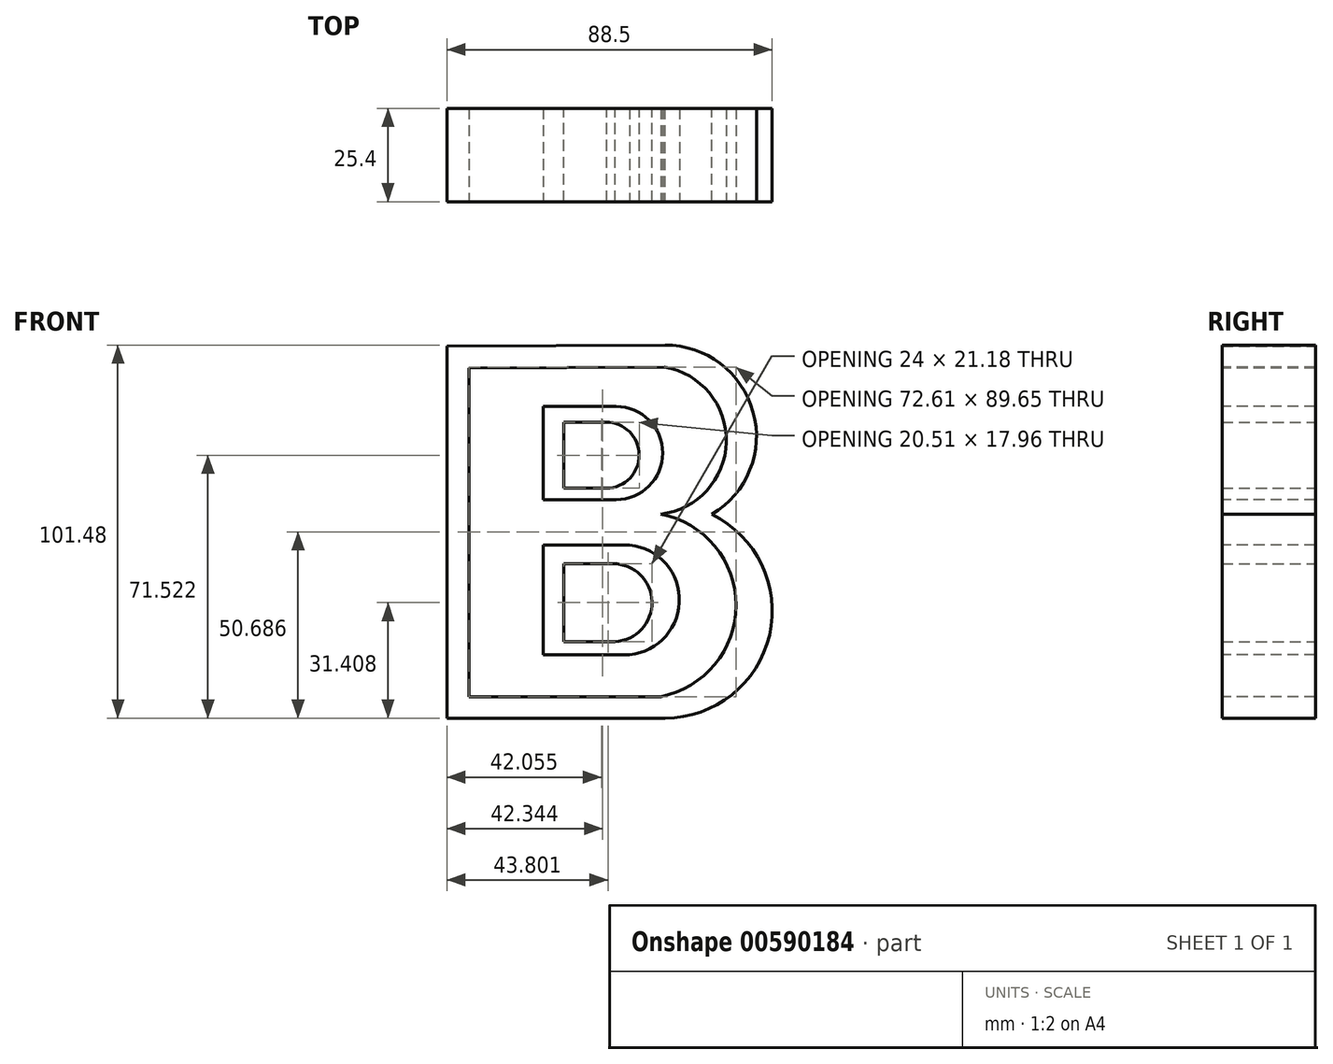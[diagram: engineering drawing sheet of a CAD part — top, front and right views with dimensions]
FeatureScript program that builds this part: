
annotation { "Feature Type Name" : "Feature", "Feature Type Description" : "" }
export const myFeature = defineFeature(function(context is Context, id is Id, definition is map)
    precondition{}
    {
        {
            var Q0;
            Q0=qCreatedBy(makeId("Front.planeOp"),FACE);
            var sketch = newSketch(context, id + "F0", { "sketchPlane" : qUnion([Q0])});
            skLineSegment(sketch, "E0", {"start": v(-89.9, 48.4) * mm, "end": v(-89.9, -52.82) * mm});
            skLineSegment(sketch, "E1", {"start": v(-89.9, -52.82) * mm, "end": v(-30.57, -52.82) * mm});
            skLineSegment(sketch, "E2", {"start": v(-30.57, 48.66) * mm, "end": v(-89.9, 48.4) * mm});
            skArc(sketch, "E3", {"start": v(-17.82, 2.6) * mm, "mid": v(-6.6, 30.5) * mm, "end": v(-30.57, 48.66) * mm});
            skArc(sketch, "E4", {"start": v(-30.57, -52.82) * mm, "mid": v(-2.14, -30.18) * mm, "end": v(-17.82, 2.6) * mm});
            skSolve(sketch);
        }
        {
            var Q0;
            Q0 = qSketchRegion(id + "F0", true);
            extrude(context, id + "F1", {"entities" : qUnion([Q0]), "depth" : 25.4 * mm, "offsetDistance" : 25.4 * mm});
        }
        {
            var Q0;
            Q0=makeQuery(id+"F0.imprint","IMPRINT",FACE,{"disambiguationData":[TD([[makeQuery(id+"F0.imprint","IMPRINT",EDGE,{"derivedFrom":sQuery(id+"F0.wireOp",EDGE,"E0")}),1.0]])]});
            var sketch = newSketch(context, id + "F2", { "sketchPlane" : qUnion([Q0])});
            skLineSegment(sketch, "E5", {"start": v(-58.1, 27.68) * mm, "end": v(-58.1, 9.72) * mm});
            skLineSegment(sketch, "E6", {"start": v(-58.1, 27.68) * mm, "end": v(-46.57, 27.68) * mm});
            skLineSegment(sketch, "E7", {"start": v(-58.1, 9.72) * mm, "end": v(-46.38, 9.72) * mm});
            skLineSegment(sketch, "E8", {"start": v(-58.1, -10.82) * mm, "end": v(-58.1, -32) * mm});
            skLineSegment(sketch, "E9", {"start": v(-58.1, -32) * mm, "end": v(-44.13, -32) * mm});
            skLineSegment(sketch, "E10", {"start": v(-58.1, -10.82) * mm, "end": v(-44.7, -10.82) * mm});
            skArc(sketch, "E11", {"start": v(-46.38, 9.72) * mm, "mid": v(-37.6, 18.8) * mm, "end": v(-46.57, 27.68) * mm});
            skArc(sketch, "E12", {"start": v(-44.13, -32) * mm, "mid": v(-34.1, -21.14) * mm, "end": v(-44.7, -10.82) * mm});
            skSolve(sketch);
        }
        {
            var Q0;
            Q0 = qSketchRegion(id + "F2", true);
            extrude(context, id + "F3", {"entities" : qUnion([Q0]), "operationType" : NewBodyOperationType.REMOVE, "oppositeDirection" : true, "depth" : 25.4 * mm, "offsetDistance" : 25.4 * mm});
        }
        {
            var Q0;
            Q0 = qSketchRegion(id + "F2", true);
            extrude(context, id + "F4", {"entities" : qUnion([Q0]), "operationType" : NewBodyOperationType.REMOVE, "depth" : 53.85 * mm, "offsetDistance" : 25.4 * mm});
        }
        {
            var Q0;
            Q0=makeQuery(id+"F1.opExtrude","CAP_FACE",FACE,{"disambiguationData":[OSD([sQuery(id+"F0.wireOp",EDGE,"E0"),sQuery(id+"F0.wireOp",EDGE,"E1"),sQuery(id+"F0.wireOp",EDGE,"E2"),sQuery(id+"F0.wireOp",EDGE,"E3"),sQuery(id+"F0.wireOp",EDGE,"E4")])],"isStart":false});
            var sketch = newSketch(context, id + "F5", { "sketchPlane" : qUnion([Q0])});
            skLineSegment(sketch, "E13", {"start": v(-83.86, 42.46) * mm, "end": v(-83.86, -46.96) * mm});
            skLineSegment(sketch, "E14", {"start": v(-83.86, -46.96) * mm, "end": v(-31.74, -46.96) * mm});
            skLineSegment(sketch, "E15", {"start": v(-83.86, 42.46) * mm, "end": v(-30.7, 42.7) * mm});
            skLineSegment(sketch, "E16", {"start": v(-63.67, 31.95) * mm, "end": v(-63.67, 6.6) * mm});
            skLineSegment(sketch, "E17", {"start": v(-63.67, 6.6) * mm, "end": v(-43.9, 6.6) * mm});
            skLineSegment(sketch, "E18", {"start": v(-63.67, -35.63) * mm, "end": v(-63.67, -5.75) * mm});
            skLineSegment(sketch, "E19", {"start": v(-63.67, -5.75) * mm, "end": v(-40.18, -5.75) * mm});
            skLineSegment(sketch, "E20", {"start": v(-63.67, -35.63) * mm, "end": v(-41.63, -35.63) * mm});
            skLineSegment(sketch, "E21", {"start": v(-63.67, 31.95) * mm, "end": v(-43.9, 31.95) * mm});
            skArc(sketch, "E22", {"start": v(-43.9, 6.6) * mm, "mid": v(-31.22, 19.28) * mm, "end": v(-43.9, 31.95) * mm});
            skArc(sketch, "E23", {"start": v(-41.63, -35.63) * mm, "mid": v(-26.67, -21.38) * mm, "end": v(-40.18, -5.75) * mm});
            skArc(sketch, "E24", {"start": v(-31.74, -46.96) * mm, "mid": v(-11.25, -22.13) * mm, "end": v(-31.74, 2.7) * mm});
            skArc(sketch, "E25", {"start": v(-31.74, 2.7) * mm, "mid": v(-13.89, 22.25) * mm, "end": v(-30.7, 42.7) * mm});
            skSolve(sketch);
        }
        {
            var Q0;
            Q0 = qSketchRegion(id + "F5", true);
            extrude(context, id + "F6", {"entities" : qUnion([Q0]), "operationType" : NewBodyOperationType.REMOVE, "oppositeDirection" : true, "depth" : 25.4 * mm, "offsetDistance" : 25.4 * mm});
        }
    });
